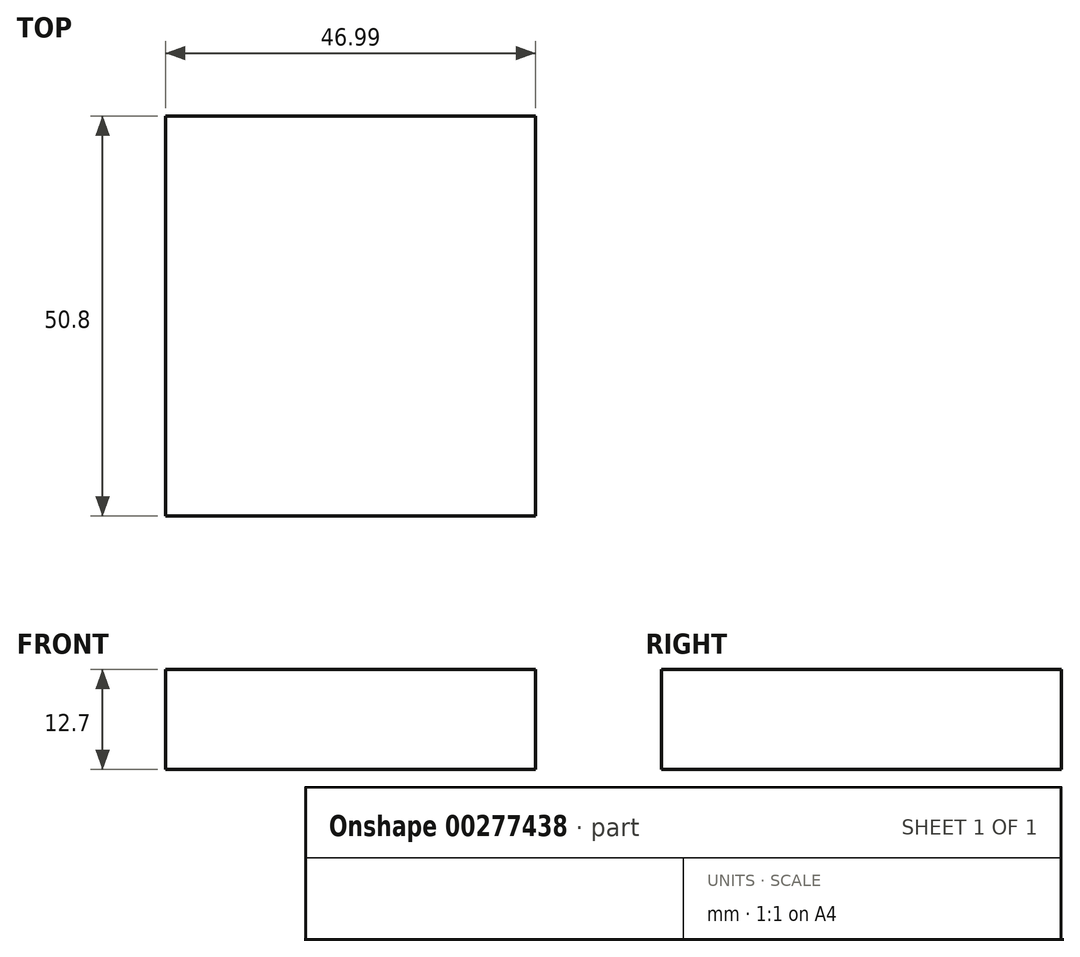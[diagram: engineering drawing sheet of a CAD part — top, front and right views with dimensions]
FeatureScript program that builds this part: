
annotation { "Feature Type Name" : "Feature", "Feature Type Description" : "" }
export const myFeature = defineFeature(function(context is Context, id is Id, definition is map)
    precondition{}
    {
        {
            var Q0;
            Q0=qCreatedBy(makeId("Top.planeOp"),FACE);
            var sketch = newSketch(context, id + "F0", { "sketchPlane" : qUnion([Q0])});
            skLineSegment(sketch, "E0.bottom", {"start": v(-19.32, -20.75) * mm, "end": v(27.67, -20.75) * mm});
            skLineSegment(sketch, "E0.top", {"start": v(-19.32, 30.05) * mm, "end": v(27.67, 30.05) * mm});
            skLineSegment(sketch, "E0.left", {"start": v(-19.32, -20.75) * mm, "end": v(-19.32, 30.05) * mm});
            skLineSegment(sketch, "E0.right", {"start": v(27.67, -20.75) * mm, "end": v(27.67, 30.05) * mm});
            skSolve(sketch);
        }
        {
            var Q0;
            Q0=makeQuery(id+"F0.imprint","IMPRINT",FACE,{"disambiguationData":[TD([[makeQuery(id+"F0.imprint","IMPRINT",EDGE,{"derivedFrom":sQuery(id+"F0.wireOp",EDGE,"E0.bottom")}),1.0]])]});
            extrude(context, id + "F1", {"entities" : qUnion([Q0]), "depth" : 12.7 * mm});
        }
    });
